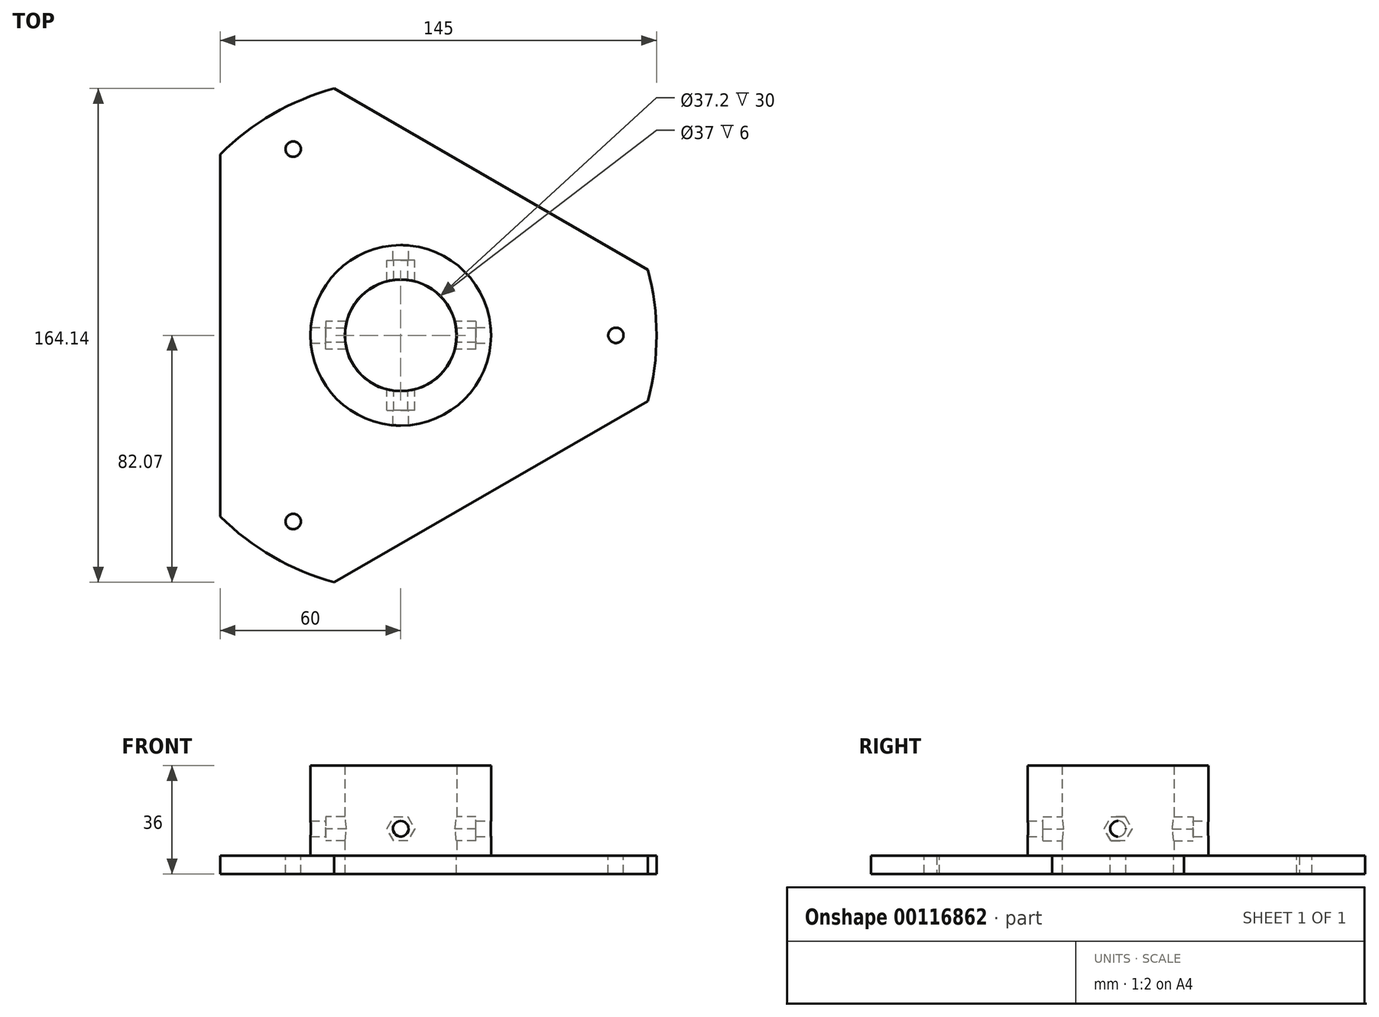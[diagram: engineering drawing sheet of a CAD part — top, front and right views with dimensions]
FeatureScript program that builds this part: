
annotation { "Feature Type Name" : "Feature", "Feature Type Description" : "" }
export const myFeature = defineFeature(function(context is Context, id is Id, definition is map)
    precondition{}
    {
        {
            var Q0;
            Q0=qCreatedBy(makeId("Top.planeOp"),FACE);
            var sketch = newSketch(context, id + "F0", { "sketchPlane" : qUnion([Q0])});
            skCircle(sketch, "E0", {"center": v(0, 0) * mm, "radius": 85 * mm});
            skCircle(sketch, "E1.cCircle", {"center": v(0, 0) * mm, "radius": 60 * mm, "construction": true});
            skLineSegment(sketch, "E1.0", {"start": v(120, 0) * mm, "end": v(-60, -103.92) * mm});
            skLineSegment(sketch, "E1.1", {"start": v(-60, -103.92) * mm, "end": v(-60, 103.92) * mm});
            skLineSegment(sketch, "E1.2", {"start": v(-60, 103.92) * mm, "end": v(120, 0) * mm});
            skPoint(sketch, "E1.0.midPoint", {"position": v(30, -51.96) * mm});
            skSolve(sketch);
        }
        {
            var Q0;
            {var subQ1=sQuery(id+"F0.wireOp",EDGE,"E0");var subQ4=sQuery(id+"F0.wireOp",EDGE,"E1.2");var subQ9=makeQuery(id+"F0.imprint","INTERSECT",VERTEX,{"disambiguationData":[OD(0.0)],"derivedFrom":[subQ1,subQ4]});Q0=makeQuery(id+"F0.imprint","IMPRINT",FACE,{"disambiguationData":[TD([[makeQuery(id+"F0.imprint","IMPRINT",EDGE,{"disambiguationData":[TD([[subQ9,-1.0]])],"derivedFrom":subQ1}),1.0]])]});}
            extrude(context, id + "F1", {"entities" : qUnion([Q0]), "depth" : 6 * mm});
        }
        {
            var Q0;
            Q0=makeQuery(id+"F1.opExtrude","CAP_FACE",FACE,{"disambiguationData":[OSD([sQuery(id+"F0.wireOp",EDGE,"E0"),sQuery(id+"F0.wireOp",EDGE,"E1.0"),sQuery(id+"F0.wireOp",EDGE,"E1.1"),sQuery(id+"F0.wireOp",EDGE,"E1.2")])],"isStart":false});
            var sketch = newSketch(context, id + "F2", { "sketchPlane" : qUnion([Q0])});
            skCircle(sketch, "E2", {"center": v(0, 0) * mm, "radius": 71.5 * mm});
            skLineSegment(sketch, "E3", {"start": v(0, 0) * mm, "end": v(118.31, 0) * mm, "construction": true});
            skCircle(sketch, "E4", {"center": v(71.5, 0) * mm, "radius": 2.55 * mm});
            skCircle(sketch, "E5.1.0", {"center": v(-35.75, 61.92) * mm, "radius": 2.55 * mm});
            skCircle(sketch, "E5.2.0", {"center": v(-35.75, -61.92) * mm, "radius": 2.55 * mm});
            skSolve(sketch);
        }
        {
            var Q0;
            {var subQ0=sQuery(id+"F2.wireOp",EDGE,"E4");var subQ1=sQuery(id+"F2.wireOp",EDGE,"E2");var subQ2=makeQuery(id+"F2.imprint","INTERSECT",VERTEX,{"disambiguationData":[OD(0.0)],"derivedFrom":[subQ1,subQ0]});Q0=makeQuery(id+"F2.imprint","IMPRINT",FACE,{"disambiguationData":[TD([[makeQuery(id+"F2.imprint","IMPRINT",EDGE,{"disambiguationData":[TD([[subQ2,1.0]])],"derivedFrom":subQ1}),1.0]])]});}
            var Q1;
            {var subQ0=sQuery(id+"F2.wireOp",EDGE,"E4");var subQ1=sQuery(id+"F2.wireOp",EDGE,"E2");var subQ2=makeQuery(id+"F2.imprint","INTERSECT",VERTEX,{"disambiguationData":[OD(0.0)],"derivedFrom":[subQ1,subQ0]});Q1=makeQuery(id+"F2.imprint","IMPRINT",FACE,{"disambiguationData":[TD([[makeQuery(id+"F2.imprint","IMPRINT",EDGE,{"disambiguationData":[TD([[subQ2,1.0]])],"derivedFrom":subQ1}),-1.0]])]});}
            var Q2;
            {var subQ0=sQuery(id+"F2.wireOp",EDGE,"E5.2.0");var subQ1=sQuery(id+"F2.wireOp",EDGE,"E2");var subQ2=makeQuery(id+"F2.imprint","INTERSECT",VERTEX,{"disambiguationData":[OD(0.0)],"derivedFrom":[subQ1,subQ0]});Q2=makeQuery(id+"F2.imprint","IMPRINT",FACE,{"disambiguationData":[TD([[makeQuery(id+"F2.imprint","IMPRINT",EDGE,{"disambiguationData":[TD([[subQ2,-1.0]])],"derivedFrom":subQ1}),-1.0]])]});}
            var Q3;
            {var subQ0=sQuery(id+"F2.wireOp",EDGE,"E5.2.0");var subQ1=sQuery(id+"F2.wireOp",EDGE,"E2");var subQ2=makeQuery(id+"F2.imprint","INTERSECT",VERTEX,{"disambiguationData":[OD(0.0)],"derivedFrom":[subQ1,subQ0]});Q3=makeQuery(id+"F2.imprint","IMPRINT",FACE,{"disambiguationData":[TD([[makeQuery(id+"F2.imprint","IMPRINT",EDGE,{"disambiguationData":[TD([[subQ2,-1.0]])],"derivedFrom":subQ1}),1.0]])]});}
            var Q4;
            {var subQ0=sQuery(id+"F2.wireOp",EDGE,"E5.1.0");var subQ1=sQuery(id+"F2.wireOp",EDGE,"E2");var subQ2=makeQuery(id+"F2.imprint","INTERSECT",VERTEX,{"disambiguationData":[OD(0.0)],"derivedFrom":[subQ1,subQ0]});Q4=makeQuery(id+"F2.imprint","IMPRINT",FACE,{"disambiguationData":[TD([[makeQuery(id+"F2.imprint","IMPRINT",EDGE,{"disambiguationData":[TD([[subQ2,-1.0]])],"derivedFrom":subQ1}),-1.0]])]});}
            var Q5;
            {var subQ0=sQuery(id+"F2.wireOp",EDGE,"E5.1.0");var subQ1=sQuery(id+"F2.wireOp",EDGE,"E2");var subQ2=makeQuery(id+"F2.imprint","INTERSECT",VERTEX,{"disambiguationData":[OD(0.0)],"derivedFrom":[subQ1,subQ0]});Q5=makeQuery(id+"F2.imprint","IMPRINT",FACE,{"disambiguationData":[TD([[makeQuery(id+"F2.imprint","IMPRINT",EDGE,{"disambiguationData":[TD([[subQ2,-1.0]])],"derivedFrom":subQ1}),1.0]])]});}
            extrude(context, id + "F3", {"entities" : qUnion([Q0, Q1, Q2, Q3, Q4, Q5]), "operationType" : NewBodyOperationType.REMOVE, "oppositeDirection" : true, "depth" : 25 * mm});
        }
        {
            var Q0;
            Q0=makeQuery(id+"F1.opExtrude","CAP_FACE",FACE,{"disambiguationData":[OSD([sQuery(id+"F0.wireOp",EDGE,"E0"),sQuery(id+"F0.wireOp",EDGE,"E1.0"),sQuery(id+"F0.wireOp",EDGE,"E1.1"),sQuery(id+"F0.wireOp",EDGE,"E1.2")])],"isStart":false});
            var sketch = newSketch(context, id + "F4", { "sketchPlane" : qUnion([Q0])});
            skCircle(sketch, "E6", {"center": v(0, 0) * mm, "radius": 18.6 * mm});
            skCircle(sketch, "E7", {"center": v(0, 0) * mm, "radius": 30 * mm});
            skSolve(sketch);
        }
        {
            var Q0;
            Q0 = qSketchRegion(id + "F4", true);
            var Q1;
            Q1=makeQuery(id+"F4.imprint","IMPRINT",FACE,{"disambiguationData":[TD([[makeQuery(id+"F4.imprint","IMPRINT",EDGE,{"derivedFrom":sQuery(id+"F4.wireOp",EDGE,"E6")}),-1.0]])]});
            extrude(context, id + "F5", {"entities" : qUnion([Q0, Q1]), "operationType" : NewBodyOperationType.ADD, "depth" : 30 * mm});
        }
        {
            var Q0;
            Q0=makeQuery(id+"F5.boolean.opBoolean","SPLIT",FACE,{"disambiguationData":[TD([makeQuery(id+"F5.opExtrude","SWEPT_FACE",FACE,{"disambiguationData":[OSD([sQuery(id+"F4.wireOp",EDGE,"E6")])]})])],"derivedFrom":makeQuery(id+"F1.opExtrude","CAP_FACE",FACE,{"disambiguationData":[OSD([sQuery(id+"F0.wireOp",EDGE,"E0"),sQuery(id+"F0.wireOp",EDGE,"E1.0"),sQuery(id+"F0.wireOp",EDGE,"E1.1"),sQuery(id+"F0.wireOp",EDGE,"E1.2")])],"isStart":false})});
            var sketch = newSketch(context, id + "F6", { "sketchPlane" : qUnion([Q0])});
            skCircle(sketch, "E8", {"center": v(0, 0) * mm, "radius": 18.5 * mm});
            skSolve(sketch);
        }
        {
            var Q0;
            Q0 = qSketchRegion(id + "F6", true);
            extrude(context, id + "F7", {"entities" : qUnion([Q0]), "operationType" : NewBodyOperationType.REMOVE, "oppositeDirection" : true, "depth" : 25 * mm});
        }
        {
            var Q0;
            Q0=qCreatedBy(makeId("Right.planeOp"),FACE);
            var sketch = newSketch(context, id + "F8", { "sketchPlane" : qUnion([Q0])});
            skLineSegment(sketch, "E9", {"start": v(0, 0) * mm, "end": v(0, 28.62) * mm, "construction": true});
            skCircle(sketch, "E10.cCircle", {"center": v(0, 15) * mm, "radius": 4 * mm, "construction": true});
            skLineSegment(sketch, "E10.0", {"start": v(2.3, 11) * mm, "end": v(-2.3, 11) * mm});
            skLineSegment(sketch, "E10.1", {"start": v(-2.3, 11) * mm, "end": v(-4.62, 15) * mm});
            skLineSegment(sketch, "E10.2", {"start": v(-4.62, 15) * mm, "end": v(-2.3, 19) * mm});
            skLineSegment(sketch, "E10.3", {"start": v(-2.3, 19) * mm, "end": v(2.3, 19) * mm});
            skLineSegment(sketch, "E10.4", {"start": v(2.3, 19) * mm, "end": v(4.62, 15) * mm});
            skLineSegment(sketch, "E10.5", {"start": v(4.62, 15) * mm, "end": v(2.3, 11) * mm});
            skPoint(sketch, "E10.0.midPoint", {"position": v(0, 11) * mm});
            skSolve(sketch);
        }
        {
            var Q0;
            Q0 = qSketchRegion(id + "F8", true);
            extrude(context, id + "F9", {"entities" : qUnion([Q0]), "operationType" : NewBodyOperationType.REMOVE, "depth" : 25 * mm, "hasSecondDirection" : true, "secondDirectionOppositeDirection" : true, "secondDirectionDepth" : 25 * mm});
        }
        {
            var Q0;
            Q0=qCreatedBy(makeId("Front.planeOp"),FACE);
            var sketch = newSketch(context, id + "F10", { "sketchPlane" : qUnion([Q0])});
            skLineSegment(sketch, "E11", {"start": v(0, 0) * mm, "end": v(0, 40) * mm, "construction": true});
            skCircle(sketch, "E12.cCircle", {"center": v(0, 15) * mm, "radius": 4 * mm, "construction": true});
            skLineSegment(sketch, "E12.0", {"start": v(2.3, 11) * mm, "end": v(-2.3, 11) * mm});
            skLineSegment(sketch, "E12.1", {"start": v(-2.3, 11) * mm, "end": v(-4.62, 15) * mm});
            skLineSegment(sketch, "E12.2", {"start": v(-4.62, 15) * mm, "end": v(-2.3, 19) * mm});
            skLineSegment(sketch, "E12.3", {"start": v(-2.3, 19) * mm, "end": v(2.3, 19) * mm});
            skLineSegment(sketch, "E12.4", {"start": v(2.3, 19) * mm, "end": v(4.62, 15) * mm});
            skLineSegment(sketch, "E12.5", {"start": v(4.62, 15) * mm, "end": v(2.3, 11) * mm});
            skPoint(sketch, "E12.0.midPoint", {"position": v(0, 11) * mm});
            skSolve(sketch);
        }
        {
            var Q0;
            Q0 = qSketchRegion(id + "F10", true);
            extrude(context, id + "F11", {"entities" : qUnion([Q0]), "operationType" : NewBodyOperationType.REMOVE, "depth" : 25 * mm, "hasSecondDirection" : true, "secondDirectionOppositeDirection" : true, "secondDirectionDepth" : 25 * mm});
        }
        {
            var Q0;
            Q0=qCreatedBy(makeId("Right.planeOp"),FACE);
            var sketch = newSketch(context, id + "F12", { "sketchPlane" : qUnion([Q0])});
            skLineSegment(sketch, "E13", {"start": v(0, 0) * mm, "end": v(0, 33.2) * mm});
            skCircle(sketch, "E14", {"center": v(0, 15) * mm, "radius": 2.6 * mm});
            skSolve(sketch);
        }
        {
            var Q0;
            Q0 = qSketchRegion(id + "F12", true);
            extrude(context, id + "F13", {"entities" : qUnion([Q0]), "operationType" : NewBodyOperationType.REMOVE, "endBound" : BoundingType.THROUGH_ALL, "oppositeDirection" : true, "depth" : 25 * mm, "hasSecondDirection" : true, "secondDirectionBound" : SecondDirectionBoundingType.THROUGH_ALL, "secondDirectionOppositeDirection" : false, "secondDirectionDepth" : 25 * mm});
        }
        {
            var Q0;
            Q0=qCreatedBy(makeId("Front.planeOp"),FACE);
            var sketch = newSketch(context, id + "F14", { "sketchPlane" : qUnion([Q0])});
            skLineSegment(sketch, "E15", {"start": v(0, 0) * mm, "end": v(0, 19.64) * mm, "construction": true});
            skCircle(sketch, "E16", {"center": v(0, 15) * mm, "radius": 2.6 * mm});
            skSolve(sketch);
        }
        {
            var Q0;
            Q0 = qSketchRegion(id + "F14", true);
            extrude(context, id + "F15", {"entities" : qUnion([Q0]), "operationType" : NewBodyOperationType.REMOVE, "endBound" : BoundingType.THROUGH_ALL, "depth" : 25 * mm, "hasSecondDirection" : true, "secondDirectionBound" : SecondDirectionBoundingType.THROUGH_ALL, "secondDirectionOppositeDirection" : true, "secondDirectionDepth" : 25 * mm});
        }
    });
